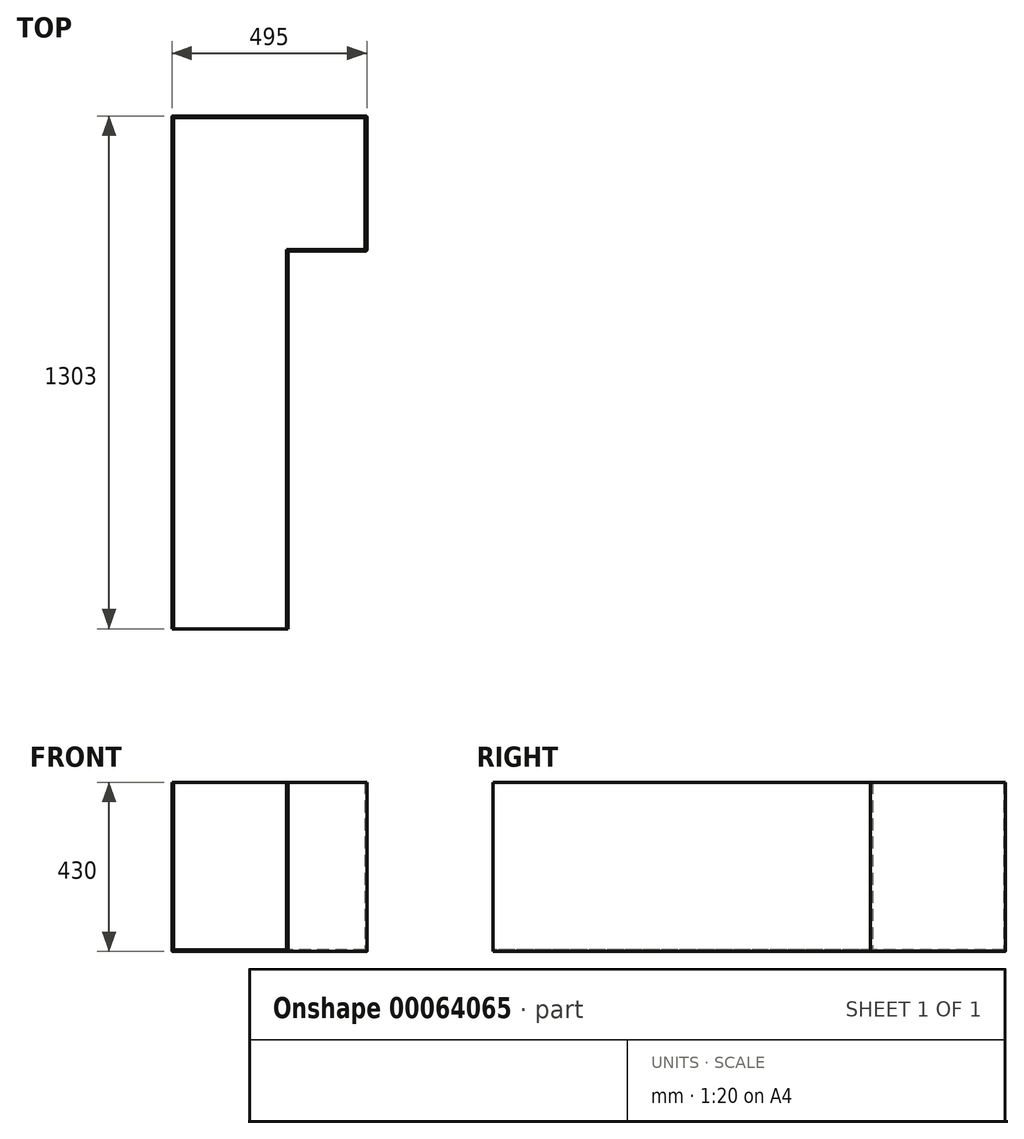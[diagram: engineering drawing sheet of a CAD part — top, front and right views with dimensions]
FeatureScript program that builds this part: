
annotation { "Feature Type Name" : "Feature", "Feature Type Description" : "" }
export const myFeature = defineFeature(function(context is Context, id is Id, definition is map)
    precondition{}
    {
        {
            var Q0;
            Q0=qCreatedBy(makeId("Top.planeOp"),FACE);
            var sketch = newSketch(context, id + "F0", { "sketchPlane" : qUnion([Q0])});
            skLineSegment(sketch, "E0", {"start": v(0, -343) * mm, "end": v(0, 0) * mm});
            skLineSegment(sketch, "E1.MirrorCS", {"start": v(-4, -339) * mm, "end": v(-4, -4) * mm});
            skLineSegment(sketch, "E2.MirrorCS", {"start": v(-4, -4) * mm, "end": v(-491, -4) * mm});
            skLineSegment(sketch, "E3.MirrorCS", {"start": v(0, 0) * mm, "end": v(-495, 0) * mm});
            skLineSegment(sketch, "E4.MirrorCS", {"start": v(-495, 0) * mm, "end": v(-495, -1303) * mm});
            skLineSegment(sketch, "E5.MirrorCS", {"start": v(-491, -4) * mm, "end": v(-491, -1303) * mm});
            skLineSegment(sketch, "E6.MirrorCS", {"start": v(-204, -339) * mm, "end": v(-204, -1303) * mm});
            skLineSegment(sketch, "E7.MirrorCS", {"start": v(-200, -343) * mm, "end": v(-200, -1303) * mm});
            skLineSegment(sketch, "E8.MirrorCS", {"start": v(-200, -343) * mm, "end": v(0, -343) * mm});
            skLineSegment(sketch, "E9.MirrorCS", {"start": v(-204, -339) * mm, "end": v(-4, -339) * mm});
            skLineSegment(sketch, "E10.MirrorCS", {"start": v(-204, -1303) * mm, "end": v(-200, -1303) * mm});
            skLineSegment(sketch, "E11.MirrorCS", {"start": v(-491, -1303) * mm, "end": v(-495, -1303) * mm});
            skSolve(sketch);
        }
        {
            var Q0;
            Q0=makeQuery(id+"F0.imprint","IMPRINT",FACE,{"disambiguationData":[TD([[makeQuery(id+"F0.imprint","IMPRINT",EDGE,{"derivedFrom":sQuery(id+"F0.wireOp",EDGE,"8549452f-c1c4-4c66-b43a-6f4cb653c117")}),-1.0]])]});
            var Q1;
            Q1=makeQuery(id+"F0.imprint","IMPRINT",FACE,{"disambiguationData":[TD([[makeQuery(id+"F0.imprint","IMPRINT",EDGE,{"derivedFrom":sQuery(id+"F0.wireOp",EDGE,"E0")}),1.0]])]});
            extrude(context, id + "F1", {"entities" : qUnion([Q0, Q1]), "depth" : 426 * mm});
        }
        {
            var Q0;
            Q0=qCreatedBy(makeId("Top.planeOp"),FACE);
            var sketch = newSketch(context, id + "F2", { "sketchPlane" : qUnion([Q0])});
            skLineSegment(sketch, "E12.0", {"start": v(-495, 0) * mm, "end": v(-495, -1303) * mm});
            skLineSegment(sketch, "E13.0", {"start": v(-200, -343) * mm, "end": v(-200, -1303) * mm});
            skLineSegment(sketch, "E14.0", {"start": v(-200, -343) * mm, "end": v(0, -343) * mm});
            skLineSegment(sketch, "E15.0", {"start": v(0, -343) * mm, "end": v(0, 0) * mm});
            skLineSegment(sketch, "E16.0", {"start": v(0, 0) * mm, "end": v(-495, 0) * mm});
            skLineSegment(sketch, "E17", {"start": v(-495, -1303) * mm, "end": v(-200, -1303) * mm});
            skSolve(sketch);
        }
        {
            var Q0;
            Q0=qSketchRegion(id+"F2",true);
            extrude(context, id + "F3", {"entities" : qUnion([Q0]), "operationType" : NewBodyOperationType.ADD, "oppositeDirection" : true, "depth" : 4 * mm});
        }
        {
            var Q0;
            Q0=makeQuery(id+"F3.opExtrude","CAP_EDGE",EDGE,{"disambiguationData":[OSD([sQuery(id+"F2.wireOp",EDGE,"e938920c-2318-497f-93e0-1fca7233731b.0")])],"isStart":false});
            var Q1;
            Q1=makeQuery(id+"F3.opExtrude","CAP_EDGE",EDGE,{"disambiguationData":[OSD([sQuery(id+"F2.wireOp",EDGE,"532a1349-e9fd-433e-8e1a-d463d1cb9540.0")])],"isStart":false});
            var Q2;
            Q2=makeQuery(id+"F3.opExtrude","CAP_EDGE",EDGE,{"disambiguationData":[OSD([sQuery(id+"F2.wireOp",EDGE,"f0b50a9b-8d41-4045-a57e-6e178546da08.0")])],"isStart":false});
            var Q3;
            Q3=makeQuery(id+"F3.opExtrude","CAP_EDGE",EDGE,{"disambiguationData":[OSD([sQuery(id+"F2.wireOp",EDGE,"76214740-f755-4499-b80f-307931e5da37.0")])],"isStart":false});
            var Q4;
            Q4=makeQuery(id+"F3.opExtrude","CAP_EDGE",EDGE,{"disambiguationData":[OSD([sQuery(id+"F2.wireOp",EDGE,"6fd2c64b-65cd-4597-b900-bc871f9f6c80.0")])],"isStart":false});
            var Q5;
            Q5=makeQuery(id+"F3.boolean.opBoolean","MERGE",EDGE,{"derivedFrom":[makeQuery(id+"F1.opExtrude","SWEPT_EDGE",EDGE,{"disambiguationData":[OSD([sQuery(id+"F0.wireOp",EDGE,"602087cb-8138-4325-86e3-c2d552e206f1"),sQuery(id+"F0.wireOp",EDGE,"5e85e9da-74ab-4066-82e7-4eeec8f45a40.right")])]}),makeQuery(id+"F3.opExtrude","SWEPT_EDGE",EDGE,{"disambiguationData":[OSD([sQuery(id+"F2.wireOp",EDGE,"532a1349-e9fd-433e-8e1a-d463d1cb9540.0"),sQuery(id+"F2.wireOp",EDGE,"f0b50a9b-8d41-4045-a57e-6e178546da08.0")])]})]});
            var Q6;
            Q6=makeQuery(id+"F3.boolean.opBoolean","MERGE",EDGE,{"derivedFrom":[makeQuery(id+"F1.opExtrude","SWEPT_EDGE",EDGE,{"disambiguationData":[OSD([sQuery(id+"F0.wireOp",EDGE,"602087cb-8138-4325-86e3-c2d552e206f1"),sQuery(id+"F0.wireOp",EDGE,"E0")])]}),makeQuery(id+"F3.opExtrude","SWEPT_EDGE",EDGE,{"disambiguationData":[OSD([sQuery(id+"F2.wireOp",EDGE,"532a1349-e9fd-433e-8e1a-d463d1cb9540.0"),sQuery(id+"F2.wireOp",EDGE,"76214740-f755-4499-b80f-307931e5da37.0")])]})]});
            var Q7;
            Q7=makeQuery(id+"F3.boolean.opBoolean","MERGE",EDGE,{"derivedFrom":[makeQuery(id+"F1.opExtrude","SWEPT_EDGE",EDGE,{"disambiguationData":[OSD([sQuery(id+"F0.wireOp",EDGE,"8549452f-c1c4-4c66-b43a-6f4cb653c117"),sQuery(id+"F0.wireOp",EDGE,"E0")])]}),makeQuery(id+"F3.opExtrude","SWEPT_EDGE",EDGE,{"disambiguationData":[OSD([sQuery(id+"F2.wireOp",EDGE,"76214740-f755-4499-b80f-307931e5da37.0"),sQuery(id+"F2.wireOp",EDGE,"6fd2c64b-65cd-4597-b900-bc871f9f6c80.0")])]})]});
            var Q8;
            Q8=makeQuery(id+"F1.opExtrude","SWEPT_EDGE",EDGE,{"disambiguationData":[OSD([sQuery(id+"F0.wireOp",EDGE,"41269a5a-69f6-4670-b1a7-19bf830e781a"),sQuery(id+"F0.wireOp",EDGE,"c0483dde-b345-4eca-95c5-d6ec0a503eff.right")])]});
            var Q9;
            Q9=makeQuery(id+"F1.opExtrude","SWEPT_EDGE",EDGE,{"disambiguationData":[OSD([sQuery(id+"F0.wireOp",EDGE,"cc5772d9-c29a-4c81-bde5-837d5d9decb7"),sQuery(id+"F0.wireOp",EDGE,"5e85e9da-74ab-4066-82e7-4eeec8f45a40.left")])]});
            var Q10;
            Q10=makeQuery(id+"F1.opExtrude","SWEPT_EDGE",EDGE,{"disambiguationData":[OSD([sQuery(id+"F0.wireOp",EDGE,"41269a5a-69f6-4670-b1a7-19bf830e781a"),sQuery(id+"F0.wireOp",EDGE,"05cfef9b-c223-4bdb-b400-77ea615546ad")])]});
            var Q11;
            Q11=makeQuery(id+"F1.opExtrude","SWEPT_EDGE",EDGE,{"disambiguationData":[OSD([sQuery(id+"F0.wireOp",EDGE,"05cfef9b-c223-4bdb-b400-77ea615546ad"),sQuery(id+"F0.wireOp",EDGE,"cc5772d9-c29a-4c81-bde5-837d5d9decb7")])]});
            var Q12;
            Q12=makeQuery(id+"F3.boolean.opBoolean","MERGE",EDGE,{"derivedFrom":[makeQuery(id+"F1.opExtrude","SWEPT_EDGE",EDGE,{"disambiguationData":[OSD([sQuery(id+"F0.wireOp",EDGE,"8549452f-c1c4-4c66-b43a-6f4cb653c117"),sQuery(id+"F0.wireOp",EDGE,"c0483dde-b345-4eca-95c5-d6ec0a503eff.left")])]}),makeQuery(id+"F3.opExtrude","SWEPT_EDGE",EDGE,{"disambiguationData":[OSD([sQuery(id+"F2.wireOp",EDGE,"6fd2c64b-65cd-4597-b900-bc871f9f6c80.0"),sQuery(id+"F2.wireOp",EDGE,"e938920c-2318-497f-93e0-1fca7233731b.0")])]})]});
            var Q13;
            Q13=makeQuery(id+"F3.opExtrude","CAP_EDGE",EDGE,{"disambiguationData":[OSD([sQuery(id+"F2.wireOp",EDGE,"E13.0")])],"isStart":false});
            var Q14;
            Q14=makeQuery(id+"F3.opExtrude","CAP_EDGE",EDGE,{"disambiguationData":[OSD([sQuery(id+"F2.wireOp",EDGE,"E12.0")])],"isStart":false});
            var Q15;
            Q15=makeQuery(id+"F3.opExtrude","CAP_EDGE",EDGE,{"disambiguationData":[OSD([sQuery(id+"F2.wireOp",EDGE,"E16.0")])],"isStart":false});
            var Q16;
            Q16=makeQuery(id+"F3.boolean.opBoolean","MERGE",EDGE,{"derivedFrom":[makeQuery(id+"F1.opExtrude","SWEPT_EDGE",EDGE,{"disambiguationData":[OSD([sQuery(id+"F0.wireOp",EDGE,"E3.MirrorCS"),sQuery(id+"F0.wireOp",EDGE,"E4.MirrorCS")])]}),makeQuery(id+"F3.opExtrude","SWEPT_EDGE",EDGE,{"disambiguationData":[OSD([sQuery(id+"F2.wireOp",EDGE,"E12.0"),sQuery(id+"F2.wireOp",EDGE,"E16.0")])]})]});
            fillet(context, id + "F4", {"entities" : qUnion([Q0, Q1, Q2, Q3, Q4, Q5, Q6, Q7, Q8, Q9, Q10, Q11, Q12, Q13, Q14, Q15, Q16]), "radius" : 2 * mm, "tangentPropagation" : true, "allowEdgeOverflow" : false});
        }
    });
